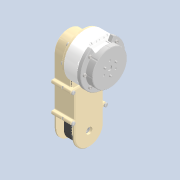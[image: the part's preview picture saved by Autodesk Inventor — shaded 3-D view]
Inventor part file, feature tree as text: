
AUTODESK INVENTOR PART (.ipt)
format: ipt  version: 2020.2 (Build 242310000, 310)  size: 5,704,704 bytes
history: native  units: in
note: dims shown in document units (in); Inventor stores cm internally (conversion verified against a paired STEP export)
features: other x64, move_body x3, extrude x1, sketch x1
ambient origin geometry x8: Origin, YZ Plane, XZ Plane, XY Plane, X Axis, Y Axis, Z Axis, Center Point
bodies: Solid1 (feature_tree)
feature tree (69):
  other  "Ensamble Final.iam"
  other  "Acople Muslo.ipt:1"
  other  "DIN 963 - M4 x 16.ipt:1"
  other  "DIN 963 - M4 x 16.ipt:2"
  other  "DIN 963 - M4 x 16.ipt:3"
  other  "DIN 912 - M4 x 0,7 x 12 x 10,25.ipt:1"
  other  "DIN 912 - M4 x 0,7 x 12 x 10,25.ipt:2"
  other  "DIN 912 - M4 x 0,7 x 12 x 10,25.ipt:3"
  other  "DIN 912 - M4 x 0,7 x 12 x 10,25.ipt:4"
  other  "DIN 912 - M4 x 0,7 x 12 x 10,25.ipt:5"
  other  "DIN 912 - M4 x 0,7 x 12 x 10,25.ipt:6"
  other  "DIN 912 - M4 x 0,7 x 12 x 10,25.ipt:7"
  other  "Cubierta Externa 1.ipt:1"
  other  "Cubierta Externa 2.ipt:1"
  other  "Polea 1.ipt:1"
  other  "DIN 7985 (H) - M4x10-H.ipt:1"
  other  "DIN 7985 (H) - M4x10-H.ipt:2"
  other  "DIN 7985 (H) - M4x10-H.ipt:3"
  other  "DIN 7985 (H) - M4x10-H.ipt:4"
  other  "DIN 125 - A 5,3.ipt:1"
  other  "DIN 125 - A 5,3.ipt:2"
  other  "DIN 125 - A 5,3.ipt:3"
  other  "DIN 7985 (H) - M4x25-H.ipt:1"
  other  "DIN 7985 (H) - M4x25-H.ipt:2"
  other  "DIN 7985 (H) - M4x25-H.ipt:3"
  other  "SKF_W 61801-2RS1.iam:1::SKF_W 61801-2RS1_PART1.ipt:1"
  other  "SKF_W 61801-2RS1.iam:1::SKF_W 61801-2RS1_PART2.ipt:1"
  other  "SKF_W 61801-2RS1.iam:1::SKF_W 61801-2RS1_PART3.ipt:1"
  other  "SKF_W 61801-2RS1.iam:1::SKF_W 61801-2RS1_PART3.ipt:2"
  other  "SKF_W 61801-2RS1.iam:1::SKF_W 61801-2RS1_PART3.ipt:3"
  other  "SKF_W 61801-2RS1.iam:1::SKF_W 61801-2RS1_PART3.ipt:4"
  other  "SKF_W 61801-2RS1.iam:1::SKF_W 61801-2RS1_PART3.ipt:5"
  other  "SKF_W 61801-2RS1.iam:1::SKF_W 61801-2RS1_PART3.ipt:6"
  other  "SKF_W 61801-2RS1.iam:1::SKF_W 61801-2RS1_PART3.ipt:7"
  other  "SKF_W 61801-2RS1.iam:1::SKF_W 61801-2RS1_PART3.ipt:8"
  other  "SKF_W 61801-2RS1.iam:1::SKF_W 61801-2RS1_PART3.ipt:9"
  other  "SKF_W 61801-2RS1.iam:1::SKF_W 61801-2RS1_PART3.ipt:10"
  other  "SKF_W 61801-2RS1.iam:1::SKF_W 61801-2RS1_PART3.ipt:11"
  other  "SKF_W 61801-2RS1.iam:1::SKF_W 61801-2RS1_PART3.ipt:12"
  other  "SKF_W 61801-2RS1.iam:2::SKF_W 61801-2RS1_PART1.ipt:1"
  other  "SKF_W 61801-2RS1.iam:2::SKF_W 61801-2RS1_PART2.ipt:1"
  other  "SKF_W 61801-2RS1.iam:2::SKF_W 61801-2RS1_PART3.ipt:1"
  other  "SKF_W 61801-2RS1.iam:2::SKF_W 61801-2RS1_PART3.ipt:2"
  other  "SKF_W 61801-2RS1.iam:2::SKF_W 61801-2RS1_PART3.ipt:3"
  other  "SKF_W 61801-2RS1.iam:2::SKF_W 61801-2RS1_PART3.ipt:4"
  other  "SKF_W 61801-2RS1.iam:2::SKF_W 61801-2RS1_PART3.ipt:5"
  other  "SKF_W 61801-2RS1.iam:2::SKF_W 61801-2RS1_PART3.ipt:6"
  other  "SKF_W 61801-2RS1.iam:2::SKF_W 61801-2RS1_PART3.ipt:7"
  other  "SKF_W 61801-2RS1.iam:2::SKF_W 61801-2RS1_PART3.ipt:8"
  other  "SKF_W 61801-2RS1.iam:2::SKF_W 61801-2RS1_PART3.ipt:9"
  other  "SKF_W 61801-2RS1.iam:2::SKF_W 61801-2RS1_PART3.ipt:10"
  other  "SKF_W 61801-2RS1.iam:2::SKF_W 61801-2RS1_PART3.ipt:11"
  other  "SKF_W 61801-2RS1.iam:2::SKF_W 61801-2RS1_PART3.ipt:12"
  other  "Ensamble Pierna.Arnés13.iam:1::Ensamble Pierna.Arnés13.ipt:1"
  other  "Motor.ipt:3"
  other  "DIN 7985 (H) - M4x22-H.ipt:1"
  other  "DIN 7985 (H) - M4x22-H.ipt:2"
  other  "DIN 7985 (H) - M4x22-H.ipt:3"
  other  "DIN 7985 (H) - M4x22-H.ipt:4"
  other  "Correa.ipt:1"
  other  "DIN 934 - M4 x 0,7.ipt:1"
  other  "DIN 934 - M4 x 0,7.ipt:2"
  other  "DIN 934 - M4 x 0,7.ipt:3"
  other  "DIN 934 - M4 x 0,7.ipt:4"
  extrude  "Extrusion1"  Depth=0.3937in TaperAngle=0.0deg
  move_body  "Move Body1"
  move_body  "Move Body2"
  move_body  "Move Body3"
  sketch  "Sketch1"  dims[d0=0.3937in d1=0.1in d2=0.0in d3=2.8022in d4=-8.5765in d5=0.0in d6=90.0deg d7=0.0in d8=0.0in d9=9.3639in]
